# Revit family: Door_Coiling_UltiGroup_UltiRollPlus_HighSpeedDoor
name_source: partatom
category: Doors
revit_build: Autodesk Revit 2018 (Build: 20170223_1515(x64)
units: mm (PartAtom-declared; Revit-internal decimal feet)

## family parameters
Always vertical = Yes
Cut with Voids When Loaded = No
Host = Wall
OmniClass Number = 23.30.10.17.27.11
OmniClass Title = Overhead Coiling
Room Calculation Point = No
Shared = No

## types (1)
- Type 1
    AccessoryOptions = Contact Manufacturer
    Analytic Construction = <None>
    AntiFingerTrapRequirement = No
    AssetType = Fixed
    BIMObjectName = Door_Coiling_UltiGroup_UltiRollPlus_HighSpeedDoor
    BreakoutFacility = No
    CB Accesories 1 = Ulti_Group_CB_Accessories_1
    CB Accessories 2 = Ulti_Group_CB_Accessories_2
    CB Accessories 3 = Ulti_Group_CB_Accessories_3
    CanopyHeightOptions = 350mm x 350mm
    Color = RAL colour options available, Contact Manufacturer
    Control Box = Ulti_Group_Control_Box_Finish
    Control Box Height = 1200 mm
    Curtain Bottom Edge = Ulti_Group_Curtain_Bottom_Edge
    CurtainMaterial = Anti-rip Cloth coated by PVC
    CurtainResistanceToBreaking = Category 1 hurricane rated up to 170 km/hr. Class 4 (Size
dependent).
    CurtainResistanceToTearing = Category 1 hurricane rated up to 170 km/hr. Class 4 (Size
dependent).
    CurtainWeightPerUnitArea = 0.90 kg/m²
    Cylinder Holder = Ulti_Group_Galvanized_Steel_Color_Black
    Description = High Speed Door
    Door Bottom height = 0 mm  [stored 0 ft]
    Door Frame Material = Ulti_Group_Door_Frame_Finish
    Door Overhead Hood Material = Ulti_Group_Door_Overhead_Hood_Material
    Door Panel Material = Ulti_Group_Curtain_Color
    DoorIncluded = No
    DoorSeal = No
    DoorsetFasteners = Screws
    DoorsetOperation = Automatic
    DoorsetOptions = Contact Manufacturer
    DurationUnit = year
    ElectricMotorEfficiency = 0
    ElectricalDeviceNominalPower = 0
    ElectronicLock = No
    Finish = Powder coated
    FireExit = No
    Format = Roll up
    FrameFinishOptions = Painted RAL colour options
    FrameMaterial = Galvanized Steel or Stainless Steel
    FrameProfile = Bent Galvanized Steel
    FrameSeal = No
    FrameSize = 125mm x 100mm
    Function = Interior
    GlassLayers = 0
    GlassType = No Glass
    GlazingAreaFraction = 0
    HandicapAccessible = Yes
    HasDrive = Yes
    HasPartWinding = No
    HasProtectiveEarth = Yes
    Head Clearance = 550 mm
    Height = 3000 mm  [stored 9.84252 ft]
    HeightUnderCanopyOptions = Clear Opening height + 200mm
    Hood Cover depth = 350 mm  [stored 1.14829 ft]
    Hood Cover height = 350 mm  [stored 1.14829 ft]
    IfcExportAs = IfcDoorStyle
    IfcExportType = Door
    Infiltration = 0
    IsExternal = No
    IsGuarded = No
    LeafColourOptions = RAL colour options available, Contact Manufacturer
    LockedRotorCurrent = 0
    Manufacturer = Ulti Group Ltd
    ManufacturerName = Ulti Group Ltd
    ManufacturerURL = www.ultigroup.co.nz
    Material = Galvanized Steel
    MaximumPowerOutput = 0
    Model = Ulti Roll Plus High Speed Door
    ModelReference = Depends on the configuration
    Motor = Ulti_Group_Motor_Cover_Finish
    Motor Casing height = 520 mm  [stored 1.70604 ft]
    Motor Casing width = 210 mm  [stored 0.688976 ft]
    Name = Door_Coiling_UltiGroup_UltiRollPlus_HighSpeedDoor
    NominalCurrent = 0
    NominalHeight = 3000 mm  [stored 9.84252 ft]
    NominalLength = 0 mm  [stored 0 ft]
    NominalVoltage = 220
    NominalWidth = 2500 mm  [stored 8.2021 ft]
    NumberOfPoles = 0
    OperatingTemperature = -30°C to +70°C
    Operation = Automatic
    OperationMode = Automatic with manual operation (chain or hand crank) in event of power failure
    PassageWidthOptions = Maximum 6000mm
    PhaseAngle = 0.00°
    Pneumatic Cylinder = Ulti_Group_Aluminium_Alloy_Material
    ProductInformation = http://ultigroup.co.nz
    SafetyDevices = Soft ballasted bottom edge
    SelfClosing = Yes
    Shape = Rectangular
    Size = Up to 6000mm x 6000mm
    SmokeStop = No
    SpeedMinimumClosing = 0.8 m/s
    SpeedMinimumOpening = 2.5 m/s
    StartCurrentFactor = 0
    ThermalTransmittance = 0
    ThresholdRequired = No
    ThresholdStripping = No
    URL = www.ultigroup.co.nz
    UsageCurrent = 0
    VP Side spacing = 300 mm
    Vision Panel = Ulti_Group_Vision_Panel_Material
    Vision Panel Bottom height = 1285 mm  [stored 4.21588 ft]
    Vision Panel height = 500 mm  [stored 1.64042 ft]
    Vision Panel height spacing = 250 mm  [stored 0.82021 ft]
    Vision Panel width = 800 mm  [stored 2.62467 ft]
    Wall Closure = By host
    WarrantyDurationLabor = 24 months labor and parts warranty
    WarrantyDurationParts = 24 months
    WarrantyDurationUnit = 24 months
    Weight = Depends on configuration and size
    Width = 2500 mm  [stored 8.2021 ft]
    WindLoadResistance = Category 1 hurricane rated up to 170 km/hr. Class 4 (Size
dependent).
    With Vision Panel = No

note: [stored X ft] marks values corroborated as IEEE doubles in the binary element streams (Revit-internal decimal feet)

## geometry (parser evidence)
native form markers: Blend x2, Sweep x2
no freeform markers — native parametric forms only
